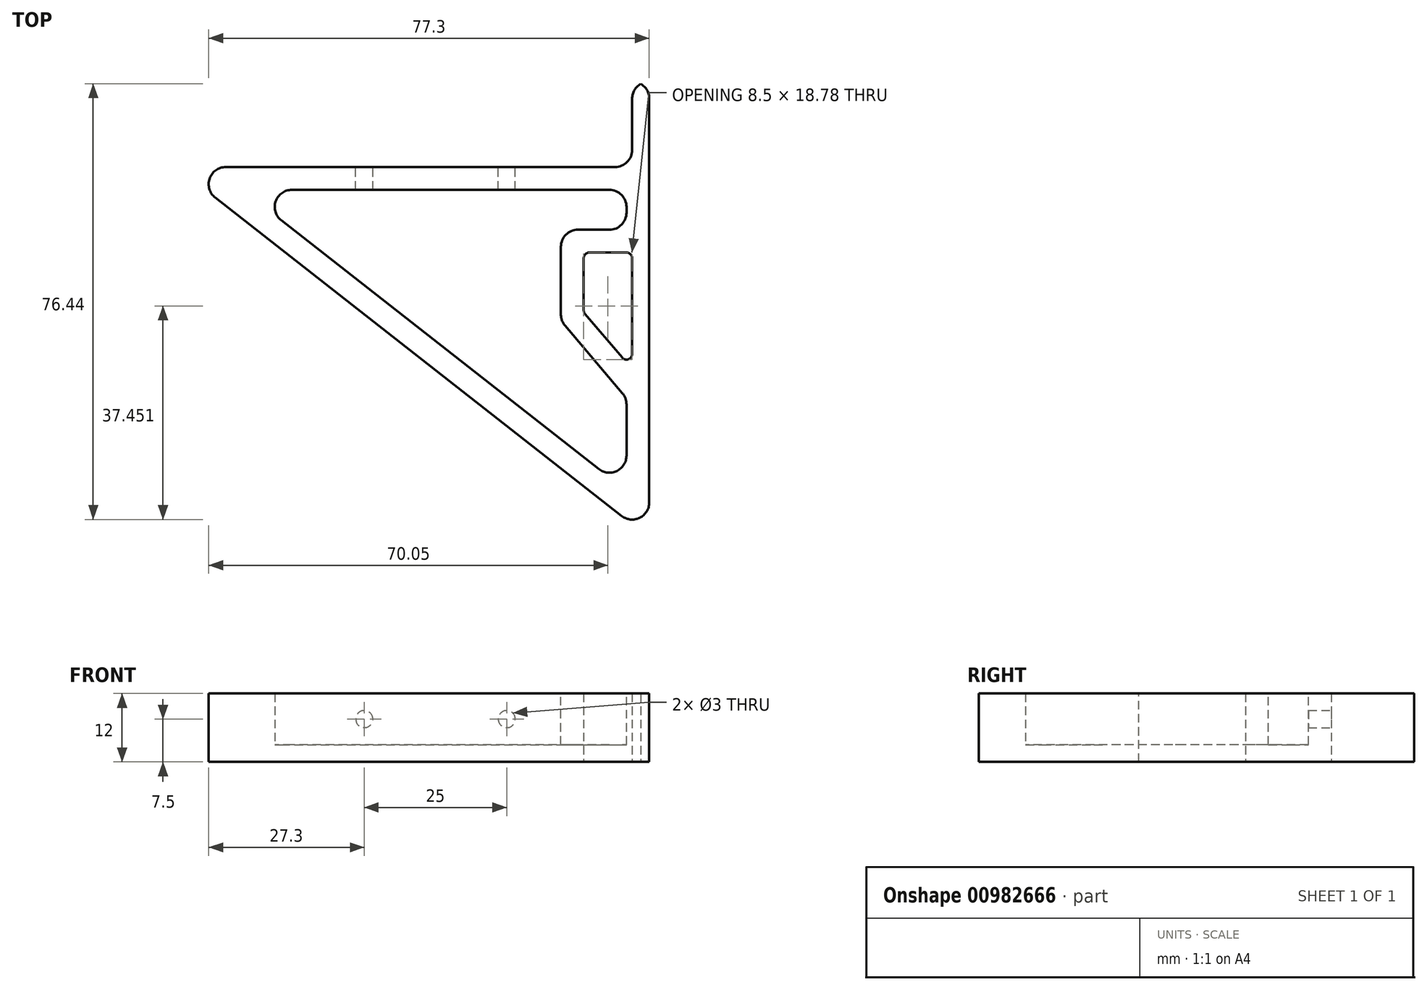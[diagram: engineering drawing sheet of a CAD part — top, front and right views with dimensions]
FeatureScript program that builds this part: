
annotation { "Feature Type Name" : "Feature", "Feature Type Description" : "" }
export const myFeature = defineFeature(function(context is Context, id is Id, definition is map)
    precondition{}
    {
        {
            var Q0;
            Q0=qCreatedBy(makeId("Top.planeOp"),FACE);
            var sketch = newSketch(context, id + "F0", { "sketchPlane" : qUnion([Q0])});
            skLineSegment(sketch, "E0", {"start": v(0, 0) * mm, "end": v(0, 80) * mm});
            skLineSegment(sketch, "E1", {"start": v(0, 80) * mm, "end": v(-3, 80) * mm});
            skLineSegment(sketch, "E2", {"start": v(-3, 80) * mm, "end": v(-3, 65) * mm});
            skLineSegment(sketch, "E3", {"start": v(-3, 65) * mm, "end": v(-83, 65) * mm});
            skLineSegment(sketch, "E4", {"start": v(-83, 65) * mm, "end": v(0, 0) * mm});
            skLineSegment(sketch, "E5", {"start": v(-3, 50) * mm, "end": v(-11.5, 50) * mm});
            skLineSegment(sketch, "E6", {"start": v(-11.5, 50) * mm, "end": v(-11.5, 39.5) * mm});
            skLineSegment(sketch, "E7", {"start": v(-11.5, 39.5) * mm, "end": v(-3, 29.5) * mm});
            skLineSegment(sketch, "E8", {"start": v(-3, 29.5) * mm, "end": v(-3, 50) * mm});
            skSolve(sketch);
        }
        {
            var Q0;
            Q0=makeQuery(id+"F0.imprint","IMPRINT",FACE,{"disambiguationData":[TD([[makeQuery(id+"F0.imprint","IMPRINT",EDGE,{"derivedFrom":sQuery(id+"F0.wireOp",EDGE,"E0")}),1.0]])]});
            extrude(context, id + "F1", {"entities" : qUnion([Q0]), "depth" : 12 * mm, "offsetDistance" : 25 * mm});
        }
        {
            var Q0;
            Q0=makeQuery(id+"F1.opExtrude","CAP_FACE",FACE,{"disambiguationData":[OSD([sQuery(id+"F0.wireOp",EDGE,"E0"),sQuery(id+"F0.wireOp",EDGE,"E1"),sQuery(id+"F0.wireOp",EDGE,"E2"),sQuery(id+"F0.wireOp",EDGE,"E3"),sQuery(id+"F0.wireOp",EDGE,"E4"),sQuery(id+"F0.wireOp",EDGE,"E5"),sQuery(id+"F0.wireOp",EDGE,"E6"),sQuery(id+"F0.wireOp",EDGE,"E7"),sQuery(id+"F0.wireOp",EDGE,"E8")])],"isStart":false});
            var sketch = newSketch(context, id + "F2", { "sketchPlane" : qUnion([Q0])});
            skLineSegment(sketch, "E9.0", {"start": v(-4, 61) * mm, "end": v(-71.4, 61) * mm});
            skLineSegment(sketch, "E10.0", {"start": v(-71.4, 61) * mm, "end": v(-4, 8.21) * mm});
            skLineSegment(sketch, "E11.0", {"start": v(-4, 54) * mm, "end": v(-15.5, 54) * mm});
            skLineSegment(sketch, "E12.0", {"start": v(-15.5, 54) * mm, "end": v(-15.5, 38.03) * mm});
            skLineSegment(sketch, "E13.0", {"start": v(-15.5, 38.03) * mm, "end": v(-4, 24.5) * mm});
            skLineSegment(sketch, "E14", {"start": v(-4, 54) * mm, "end": v(-4, 61) * mm});
            skLineSegment(sketch, "E15", {"start": v(-4, 8.21) * mm, "end": v(-4, 24.5) * mm});
            skSolve(sketch);
        }
        {
            var Q0;
            Q0=makeQuery(id+"F2.imprint","IMPRINT",FACE,{"disambiguationData":[TD([[makeQuery(id+"F2.imprint","IMPRINT",EDGE,{"derivedFrom":sQuery(id+"F2.wireOp",EDGE,"E9.0")}),1.0]])]});
            extrude(context, id + "F3", {"entities" : qUnion([Q0]), "operationType" : NewBodyOperationType.REMOVE, "oppositeDirection" : true, "depth" : 9 * mm, "offsetDistance" : 25 * mm});
        }
        {
            var Q0;
            Q0=makeQuery(id+"F1.opExtrude","SWEPT_FACE",FACE,{"disambiguationData":[OSD([sQuery(id+"F0.wireOp",EDGE,"E3")])]});
            var sketch = newSketch(context, id + "F4", { "sketchPlane" : qUnion([Q0])});
            skLineSegment(sketch, "E16", {"start": v(25, 7.5) * mm, "end": v(50, 7.5) * mm, "construction": true});
            skCircle(sketch, "E17", {"center": v(50, 7.5) * mm, "radius": 1.5 * mm});
            skCircle(sketch, "E18", {"center": v(25, 7.5) * mm, "radius": 1.5 * mm});
            skSolve(sketch);
        }
        {
            var Q0;
            Q0 = qSketchRegion(id + "F4", true);
            extrude(context, id + "F5", {"entities" : qUnion([Q0]), "operationType" : NewBodyOperationType.REMOVE, "oppositeDirection" : true, "depth" : 4 * mm, "offsetDistance" : 25 * mm});
        }
        {
            var Q0;
            Q0=makeQuery(id+"F1.opExtrude","SWEPT_EDGE",EDGE,{"disambiguationData":[OSD([sQuery(id+"F0.wireOp",EDGE,"E2"),sQuery(id+"F0.wireOp",EDGE,"E3")])]});
            var Q1;
            Q1=makeQuery(id+"F3.boolean.opBoolean","COPY",EDGE,{"derivedFrom":makeQuery(id+"F3.opExtrude","SWEPT_EDGE",EDGE,{"disambiguationData":[OSD([sQuery(id+"F2.wireOp",EDGE,"E11.0"),sQuery(id+"F2.wireOp",EDGE,"E14")])]})});
            var Q2;
            Q2=makeQuery(id+"F3.boolean.opBoolean","COPY",EDGE,{"derivedFrom":makeQuery(id+"F3.opExtrude","SWEPT_EDGE",EDGE,{"disambiguationData":[OSD([sQuery(id+"F2.wireOp",EDGE,"E11.0"),sQuery(id+"F2.wireOp",EDGE,"E12.0")])]})});
            var Q3;
            Q3=makeQuery(id+"F3.boolean.opBoolean","COPY",EDGE,{"derivedFrom":makeQuery(id+"F3.opExtrude","SWEPT_EDGE",EDGE,{"disambiguationData":[OSD([sQuery(id+"F2.wireOp",EDGE,"E9.0"),sQuery(id+"F2.wireOp",EDGE,"E14")])]})});
            var Q4;
            Q4=makeQuery(id+"F3.boolean.opBoolean","COPY",EDGE,{"derivedFrom":makeQuery(id+"F3.opExtrude","SWEPT_EDGE",EDGE,{"disambiguationData":[OSD([sQuery(id+"F2.wireOp",EDGE,"E13.0"),sQuery(id+"F2.wireOp",EDGE,"E15")])]})});
            var Q5;
            Q5=makeQuery(id+"F3.boolean.opBoolean","COPY",EDGE,{"derivedFrom":makeQuery(id+"F3.opExtrude","SWEPT_EDGE",EDGE,{"disambiguationData":[OSD([sQuery(id+"F2.wireOp",EDGE,"E12.0"),sQuery(id+"F2.wireOp",EDGE,"E13.0")])]})});
            var Q6;
            Q6=makeQuery(id+"F3.boolean.opBoolean","COPY",EDGE,{"derivedFrom":makeQuery(id+"F3.opExtrude","SWEPT_EDGE",EDGE,{"disambiguationData":[OSD([sQuery(id+"F2.wireOp",EDGE,"E10.0"),sQuery(id+"F2.wireOp",EDGE,"E15")])]})});
            var Q7;
            Q7=makeQuery(id+"F3.boolean.opBoolean","COPY",EDGE,{"derivedFrom":makeQuery(id+"F3.opExtrude","SWEPT_EDGE",EDGE,{"disambiguationData":[OSD([sQuery(id+"F2.wireOp",EDGE,"E9.0"),sQuery(id+"F2.wireOp",EDGE,"E10.0")])]})});
            var Q8;
            Q8=makeQuery(id+"F1.opExtrude","SWEPT_EDGE",EDGE,{"disambiguationData":[OSD([sQuery(id+"F0.wireOp",EDGE,"E3"),sQuery(id+"F0.wireOp",EDGE,"E4")])]});
            var Q9;
            Q9=makeQuery(id+"F1.opExtrude","SWEPT_EDGE",EDGE,{"disambiguationData":[OSD([sQuery(id+"F0.wireOp",EDGE,"E1"),sQuery(id+"F0.wireOp",EDGE,"E2")])]});
            var Q10;
            Q10=makeQuery(id+"F1.opExtrude","SWEPT_EDGE",EDGE,{"disambiguationData":[OSD([sQuery(id+"F0.wireOp",EDGE,"E0"),sQuery(id+"F0.wireOp",EDGE,"E4")])]});
            var Q11;
            Q11=makeQuery(id+"F1.opExtrude","SWEPT_EDGE",EDGE,{"disambiguationData":[OSD([sQuery(id+"F0.wireOp",EDGE,"E0"),sQuery(id+"F0.wireOp",EDGE,"E1")])]});
            fillet(context, id + "F6", {"entities" : qUnion([Q0, Q1, Q2, Q3, Q4, Q5, Q6, Q7, Q8, Q9, Q10, Q11]), "radius" : 3 * mm, "tangentPropagation" : true, "allowEdgeOverflow" : false});
        }
        {
            var Q0;
            Q0=makeQuery(id+"F1.opExtrude","SWEPT_EDGE",EDGE,{"disambiguationData":[OSD([sQuery(id+"F0.wireOp",EDGE,"E5"),sQuery(id+"F0.wireOp",EDGE,"E6")])]});
            var Q1;
            Q1=makeQuery(id+"F1.opExtrude","SWEPT_EDGE",EDGE,{"disambiguationData":[OSD([sQuery(id+"F0.wireOp",EDGE,"E5"),sQuery(id+"F0.wireOp",EDGE,"E8")])]});
            var Q2;
            Q2=makeQuery(id+"F1.opExtrude","SWEPT_EDGE",EDGE,{"disambiguationData":[OSD([sQuery(id+"F0.wireOp",EDGE,"E6"),sQuery(id+"F0.wireOp",EDGE,"E7")])]});
            var Q3;
            Q3=makeQuery(id+"F1.opExtrude","SWEPT_EDGE",EDGE,{"disambiguationData":[OSD([sQuery(id+"F0.wireOp",EDGE,"E7"),sQuery(id+"F0.wireOp",EDGE,"E8")])]});
            fillet(context, id + "F7", {"entities" : qUnion([Q0, Q1, Q2, Q3]), "radius" : 1 * mm, "tangentPropagation" : true, "allowEdgeOverflow" : false});
        }
    });
